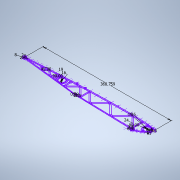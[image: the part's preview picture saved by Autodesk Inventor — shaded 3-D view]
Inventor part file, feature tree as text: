
AUTODESK INVENTOR PART (.ipt)
format: ipt  version: 2022 (Build 260153000, 153)  size: 266,752 bytes
history: native  units: mm
features: sketch x1
ambient origin geometry x8: Origin, YZ Plane, XZ Plane, XY Plane, X Axis, Y Axis, Z Axis, Center Point
feature tree (1):
  sketch  "Sketch1"  dims[d31=34.456mm d50=368.759386mm d57=16.0mm d69=8.0mm d80=19.0mm d81=16.0mm d82=1.0mm d83=1.0mm d84=1.0mm d85=1.0mm d86=1.0mm d87=0.8mm d88=1.0mm d90=19.0mm d94=5.0mm d95=5.0mm d105=5.0mm d106=5.0mm d108=2.0mm d114=5.0mm d115=5.0mm d116=24.0mm d117=2.5mm d118=2.5mm d123=2.5mm d124=2.5mm d125=10.0mm d126=24.0mm d127=24.0mm d128=27.0mm d135=0.5mm d139=7.0mm d169=27.0mm d181=45.0deg d185=7.0mm d186=45.0deg d190=7.0mm d191=45.0deg d206=90.0deg d212=90.0deg d215=7.0mm d216=90.0deg d219=7.0mm]
